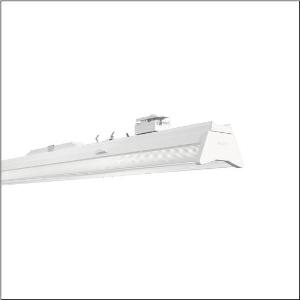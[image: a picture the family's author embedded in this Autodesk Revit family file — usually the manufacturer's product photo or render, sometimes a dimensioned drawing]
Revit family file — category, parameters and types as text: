
# Revit family: licross_r__21_performance_mo_52td16vn455g_74b2
name_source: partatom
category: Lighting Fixtures
units: mm (PartAtom-declared; Revit-internal decimal feet)

## family parameters
Cut with Voids When Loaded = No
Host = Face
Light Source = No
Part Type = Normal
Room Calculation Point = No
Round Connector Dimension = Use Diameter
Shared = No

## types (1)
- --- (1 x LED, 5500 lm, 30 W, 4000K)
    Apparent Load = 30 VA
    CIE Flux Codes = 66 88 96 79 100
    Color Rendering = 80
    Color Temperature = 4000K
    Default Elevation = 1800 mm
    Description = Licross® 21 Performance MO, luminaire insert, of sheet steel, galvanised, coil coated, white, length: 1.500mm, width: 120mm, height: 123mm, LED rated luminous flux: 5.500lm, light colour: 840, control gear: DALI 2, CLO, with plug, 5-pole, with phase selection, mains connection: 220..240V, AC, 50/60Hz, start of lifetime: 30W, end of service life: 36W, halogen-free wiring, primary light control with lens, of plastic, primary optical cover: cover, of PMMA, light emission: direct/indirect distribution, primary light characteristic: symmetric, protection rating (complete): IP54, insulation class (complete): insulation class I (protective earthing), certification: CE, ENEC, VDE, UKCA, protection symbol: D if used in an environment with non-conductive dust loads with corresponding accessories, impact resistance: IK06, permissible ambient temperature for indoor applications: -25..+50°C, corresponds to IFS (International Featured Standards) requirements for safety and quality in the food industry, reducing of maximum allowable ambient temperature of 5°C with ceiling mounting, LABS conformity tested according to VDMA 24364:2018-05, packaging unit: 1 piece
    Height = 114 mm
    Lamp = 1 x LED
    Lamp Light Flux = 5500 lm
    Lamp Power = 30 W
    Lamp count = 1
    Length = 1500 mm
    Luminous efficacy = 183 lm/W
    Manufacturer = Siteco
    ModVariant = No
    Model = 52TD16VN455G
    Mounting Place = Ceiling
    Mounting Type = Pendant
    Number of Poles = 1
    OnlyDefault = Yes
    Power Factor = 1
    Product Name = Licross® 21 Performance MO
    Product group = luminaire insert
    ProductGroupID = 901
    Protection Class = Protection class I
    Protection Degree = IP 54
    RLX_Detail_Level = 1
    RLX_Emergency_Light_Flux = 0 lm
    RLX_Emergency_Type = 0
    RLX_Emergency_Type_DB = No
    RlxData = <blob elided: 33549 chars, md5=f0760953>
    Socket = socket
    Standby Power = 0 W
    System Light Flux = 5500 lm
    System Power = 30 W
    Type Comments = factory setting: luminous flux: 100 % | dim-lin: 254 | 203 mA
    Type Image = l_1256138.jpg
    URL = http://relux.com
    VarID = @adj_078074
    Voltage = 0 V
    Weight = 0.00 kg
    Width = 120 mm

## geometry (parser evidence)
native form markers: Blend x4, Sweep x12
no freeform markers — native parametric forms only
